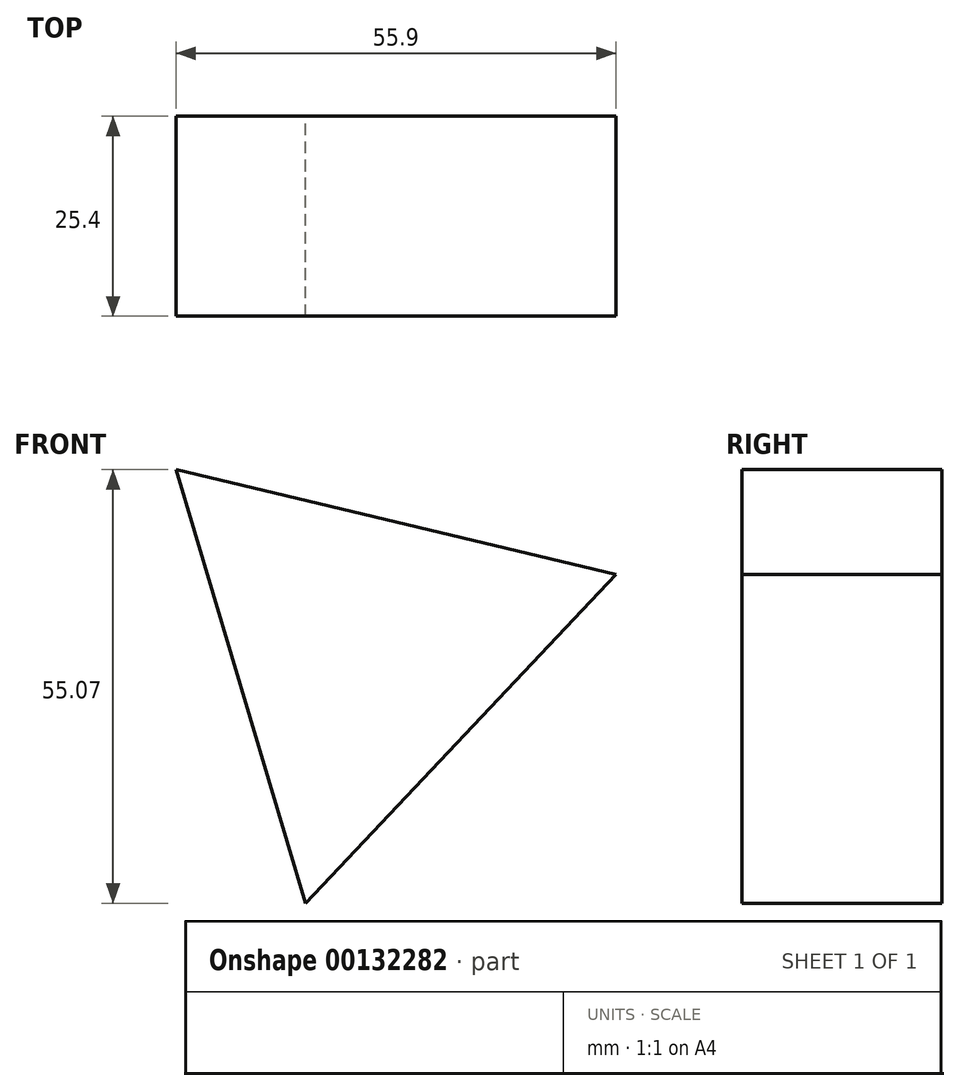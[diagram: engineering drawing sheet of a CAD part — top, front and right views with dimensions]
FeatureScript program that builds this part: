
annotation { "Feature Type Name" : "Feature", "Feature Type Description" : "" }
export const myFeature = defineFeature(function(context is Context, id is Id, definition is map)
    precondition{}
    {
        {
            var Q0;
            Q0=qCreatedBy(makeId("Front.planeOp"),FACE);
            var sketch = newSketch(context, id + "F0", { "sketchPlane" : qUnion([Q0])});
            skCircle(sketch, "E0.cCircle", {"center": v(0, 0) * mm, "radius": 33.18 * mm, "construction": true});
            skLineSegment(sketch, "E0.0", {"start": v(-24.1, 22.8) * mm, "end": v(31.8, 9.48) * mm});
            skLineSegment(sketch, "E0.1", {"start": v(31.8, 9.48) * mm, "end": v(-7.7, -32.27) * mm});
            skLineSegment(sketch, "E0.2", {"start": v(-7.7, -32.27) * mm, "end": v(-24.1, 22.8) * mm});
            skSolve(sketch);
        }
        {
            var Q0;
            Q0=makeQuery(id+"F0.imprint","IMPRINT",FACE,{"disambiguationData":[TD([[makeQuery(id+"F0.imprint","IMPRINT",EDGE,{"derivedFrom":sQuery(id+"F0.wireOp",EDGE,"E0.0")}),-1.0]])]});
            extrude(context, id + "F1", {"entities" : qUnion([Q0]), "depth" : 25.4 * mm});
        }
    });
